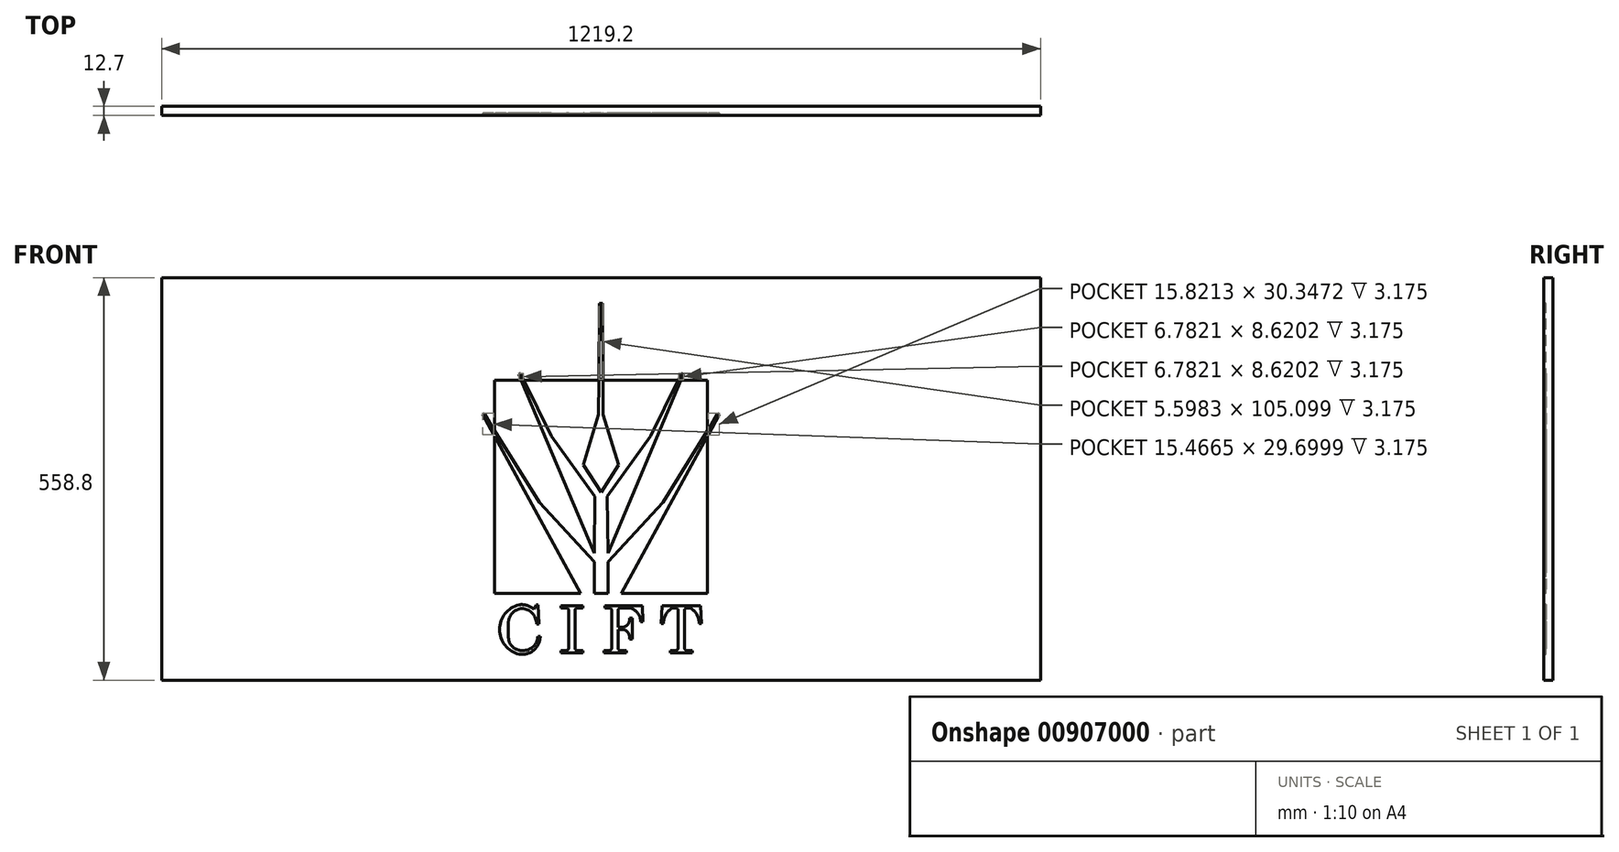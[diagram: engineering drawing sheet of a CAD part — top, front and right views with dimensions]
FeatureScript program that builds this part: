
annotation { "Feature Type Name" : "Feature", "Feature Type Description" : "" }
export const myFeature = defineFeature(function(context is Context, id is Id, definition is map)
    precondition{}
    {
        {
            var Q0;
            Q0=qCreatedBy(makeId("Front.planeOp"),FACE);
            var sketch = newSketch(context, id + "F0", { "sketchPlane" : qUnion([Q0])});
            skLineSegment(sketch, "E0.bottom", {"start": v(-609.6, 279.4) * mm, "end": v(609.6, 279.4) * mm});
            skLineSegment(sketch, "E0.top", {"start": v(-609.6, -279.4) * mm, "end": v(609.6, -279.4) * mm});
            skLineSegment(sketch, "E0.left", {"start": v(-609.6, 279.4) * mm, "end": v(-609.6, -279.4) * mm});
            skLineSegment(sketch, "E0.right", {"start": v(609.6, 279.4) * mm, "end": v(609.6, -279.4) * mm});
            skPoint(sketch, "E0.middle", {"position": v(0, 0) * mm});
            skSolve(sketch);
        }
        {
            var Q0;
            Q0=makeQuery(id+"F0.imprint","IMPRINT",FACE,{"disambiguationData":[TD([[makeQuery(id+"F0.imprint","IMPRINT",EDGE,{"derivedFrom":sQuery(id+"F0.wireOp",EDGE,"E0.bottom")}),-1.0]])]});
            extrude(context, id + "F1", {"entities" : qUnion([Q0]), "depth" : 12.7 * mm, "offsetDistance" : 25.4 * mm});
        }
        {
            var Q0;
            Q0=makeQuery(id+"F1.opExtrude","CAP_FACE",FACE,{"disambiguationData":[OSD([sQuery(id+"F0.wireOp",EDGE,"E0.bottom"),sQuery(id+"F0.wireOp",EDGE,"E0.top"),sQuery(id+"F0.wireOp",EDGE,"E0.left"),sQuery(id+"F0.wireOp",EDGE,"E0.right")])],"isStart":false});
            var sketch = newSketch(context, id + "F2", { "sketchPlane" : qUnion([Q0])});
            skLineSegment(sketch, "E1", {"start": v(-147.74, 136.91) * mm, "end": v(147.74, 136.91) * mm});
            skLineSegment(sketch, "E2", {"start": v(147.74, 136.91) * mm, "end": v(147.74, -158.78) * mm});
            skLineSegment(sketch, "E3", {"start": v(-148.88, 61.33) * mm, "end": v(-164.34, 89.54) * mm});
            skLineSegment(sketch, "E4", {"start": v(-161.78, 91.03) * mm, "end": v(-148.88, 68.77) * mm});
            skLineSegment(sketch, "E5", {"start": v(-85.66, -32.31) * mm, "end": v(-9.52, -115.33) * mm});
            skLineSegment(sketch, "E6", {"start": v(-9.52, -115.33) * mm, "end": v(-9.52, -158.78) * mm});
            skLineSegment(sketch, "E7", {"start": v(-164.34, 89.54) * mm, "end": v(-161.78, 91.03) * mm});
            skLineSegment(sketch, "E8", {"start": v(-114.28, 145.2) * mm, "end": v(-111.35, 146.3) * mm});
            skLineSegment(sketch, "E9", {"start": v(-111.35, 146.3) * mm, "end": v(-107.5, 137.68) * mm});
            skLineSegment(sketch, "E10", {"start": v(-68.91, 59.28) * mm, "end": v(-8.42, -24.15) * mm});
            skLineSegment(sketch, "E11", {"start": v(-8.42, -24.15) * mm, "end": v(-9.47, -102.91) * mm});
            skLineSegment(sketch, "E12", {"start": v(-111.1, 137.68) * mm, "end": v(-114.28, 145.2) * mm});
            skLineSegment(sketch, "E13", {"start": v(-0.06, -18.37) * mm, "end": v(-24.45, 19.7) * mm});
            skLineSegment(sketch, "E14", {"start": v(-24.45, 19.7) * mm, "end": v(-3.44, 89.6) * mm});
            skLineSegment(sketch, "E15", {"start": v(-3, 138.55) * mm, "end": v(-2.05, 243.65) * mm});
            skLineSegment(sketch, "E16", {"start": v(85.66, -32.31) * mm, "end": v(9.52, -115.33) * mm});
            skLineSegment(sketch, "E17", {"start": v(9.52, -115.33) * mm, "end": v(9.52, -158.78) * mm});
            skLineSegment(sketch, "E18", {"start": v(114.28, 145.2) * mm, "end": v(111.35, 146.3) * mm});
            skLineSegment(sketch, "E19", {"start": v(111.35, 146.3) * mm, "end": v(107.5, 137.68) * mm});
            skLineSegment(sketch, "E20", {"start": v(68.91, 59.28) * mm, "end": v(8.42, -24.15) * mm});
            skLineSegment(sketch, "E21", {"start": v(8.42, -24.15) * mm, "end": v(9.47, -102.91) * mm});
            skLineSegment(sketch, "E22", {"start": v(111.1, 137.68) * mm, "end": v(114.28, 145.2) * mm});
            skLineSegment(sketch, "E23", {"start": v(161.78, 91.03) * mm, "end": v(148.52, 68.16) * mm});
            skLineSegment(sketch, "E24", {"start": v(164.34, 89.54) * mm, "end": v(161.78, 91.03) * mm});
            skLineSegment(sketch, "E25", {"start": v(147.74, -158.78) * mm, "end": v(147.74, 136.91) * mm});
            skLineSegment(sketch, "E26", {"start": v(148.52, 60.68) * mm, "end": v(164.34, 89.54) * mm});
            skLineSegment(sketch, "E27", {"start": v(2.6, 138.55) * mm, "end": v(1.95, 243.65) * mm});
            skLineSegment(sketch, "E28", {"start": v(24.45, 19.7) * mm, "end": v(2.9, 89.6) * mm});
            skLineSegment(sketch, "E29", {"start": v(-147.74, -158.78) * mm, "end": v(-147.74, 136.91) * mm});
            skLineSegment(sketch, "E30", {"start": v(-0.06, -18.37) * mm, "end": v(24.45, 19.7) * mm});
            skLineSegment(sketch, "E31", {"start": v(-147.74, -158.78) * mm, "end": v(-28.22, -158.78) * mm});
            skLineSegment(sketch, "E32", {"start": v(28.22, -158.78) * mm, "end": v(147.74, -158.78) * mm});
            skLineSegment(sketch, "E33", {"start": v(-9.52, -158.78) * mm, "end": v(9.52, -158.78) * mm});
            skLineSegment(sketch, "E34", {"start": v(68.91, 59.28) * mm, "end": v(107.16, 136.91) * mm});
            skLineSegment(sketch, "E35", {"start": v(110.78, 136.91) * mm, "end": v(9.47, -102.91) * mm});
            skLineSegment(sketch, "E36", {"start": v(2.9, 89.6) * mm, "end": v(2.6, 136.91) * mm});
            skLineSegment(sketch, "E37", {"start": v(-3.01, 136.91) * mm, "end": v(-3.44, 89.6) * mm});
            skLineSegment(sketch, "E38", {"start": v(28.22, -158.78) * mm, "end": v(147.74, 59.25) * mm});
            skLineSegment(sketch, "E39", {"start": v(147.74, 66.8) * mm, "end": v(85.66, -32.31) * mm});
            skLineSegment(sketch, "E40", {"start": v(-68.91, 59.28) * mm, "end": v(-107.16, 136.91) * mm});
            skLineSegment(sketch, "E41", {"start": v(-110.78, 136.91) * mm, "end": v(-9.47, -102.91) * mm});
            skLineSegment(sketch, "E42", {"start": v(-85.66, -32.31) * mm, "end": v(-147.74, 66.8) * mm});
            skLineSegment(sketch, "E43", {"start": v(-147.74, 59.25) * mm, "end": v(-28.22, -158.78) * mm});
            skLineSegment(sketch, "E44", {"start": v(2.6, 136.91) * mm, "end": v(-3.01, 136.91) * mm});
            skLineSegment(sketch, "E45", {"start": v(110.78, 136.91) * mm, "end": v(107.16, 136.91) * mm});
            skLineSegment(sketch, "E46", {"start": v(147.74, 66.8) * mm, "end": v(147.74, 59.25) * mm});
            skLineSegment(sketch, "E47", {"start": v(-107.16, 136.91) * mm, "end": v(-110.78, 136.91) * mm});
            skLineSegment(sketch, "E48", {"start": v(-147.74, 59.25) * mm, "end": v(-147.74, 66.8) * mm});
            skArc(sketch, "E49", {"start": v(-89.4, -201.28) * mm, "mid": v(-95.36, -186.47) * mm, "end": v(-109.87, -179.83) * mm});
            skArc(sketch, "E50", {"start": v(-108.5, -238.28) * mm, "mid": v(-93.98, -232.57) * mm, "end": v(-87.6, -218.33) * mm});
            skLineSegment(sketch, "E51", {"start": v(-89.4, -201.28) * mm, "end": v(-86.08, -201.28) * mm});
            skLineSegment(sketch, "E52", {"start": v(-86.08, -201.28) * mm, "end": v(-87.23, -174.61) * mm});
            skLineSegment(sketch, "E53", {"start": v(-87.23, -174.61) * mm, "end": v(-90.18, -174.61) * mm});
            skLineSegment(sketch, "E54", {"start": v(-90.18, -174.61) * mm, "end": v(-93.08, -180.85) * mm});
            skLineSegment(sketch, "E55", {"start": v(-87.6, -218.33) * mm, "end": v(-84.44, -218.33) * mm});
            skArc(sketch, "E56", {"start": v(-128.45, -218.68) * mm, "mid": v(-122.82, -232.9) * mm, "end": v(-108.5, -238.28) * mm});
            skLineSegment(sketch, "E57", {"start": v(-55.67, -241.5) * mm, "end": v(-25.42, -241.5) * mm});
            skLineSegment(sketch, "E58", {"start": v(-55.67, -175.85) * mm, "end": v(-25.42, -175.85) * mm});
            skLineSegment(sketch, "E59", {"start": v(-55.67, -179.27) * mm, "end": v(-48.06, -179.27) * mm});
            skLineSegment(sketch, "E60", {"start": v(-55.67, -238.08) * mm, "end": v(-48.06, -238.08) * mm});
            skLineSegment(sketch, "E61", {"start": v(23.77, -205.82) * mm, "end": v(31.92, -205.82) * mm});
            skLineSegment(sketch, "E62", {"start": v(23.77, -209.24) * mm, "end": v(31.92, -209.24) * mm});
            skLineSegment(sketch, "E63", {"start": v(-45.08, -235.1) * mm, "end": v(-45.08, -182.24) * mm});
            skLineSegment(sketch, "E64", {"start": v(-35.9, -235.1) * mm, "end": v(-35.9, -182.24) * mm});
            skLineSegment(sketch, "E65", {"start": v(106.73, -235.1) * mm, "end": v(106.73, -182.24) * mm});
            skLineSegment(sketch, "E66", {"start": v(115.92, -235.1) * mm, "end": v(115.92, -182.24) * mm});
            skLineSegment(sketch, "E67", {"start": v(83.33, -200.72) * mm, "end": v(86.66, -200.72) * mm});
            skArc(sketch, "E68", {"start": v(98.5, -179.27) * mm, "mid": v(89.69, -188.4) * mm, "end": v(86.66, -200.72) * mm});
            skLineSegment(sketch, "E69", {"start": v(84.8, -175.85) * mm, "end": v(83.33, -200.72) * mm});
            skLineSegment(sketch, "E70", {"start": v(139.32, -200.72) * mm, "end": v(136, -200.72) * mm});
            skArc(sketch, "E71", {"start": v(136, -200.72) * mm, "mid": v(132.97, -188.4) * mm, "end": v(124.15, -179.27) * mm});
            skLineSegment(sketch, "E72", {"start": v(137.86, -175.85) * mm, "end": v(139.32, -200.72) * mm});
            skLineSegment(sketch, "E73", {"start": v(96.15, -241.5) * mm, "end": v(96.15, -238.08) * mm});
            skLineSegment(sketch, "E74", {"start": v(126.65, -241.5) * mm, "end": v(126.65, -238.08) * mm});
            skLineSegment(sketch, "E75", {"start": v(35.47, -241.5) * mm, "end": v(35.47, -238.08) * mm});
            skLineSegment(sketch, "E76", {"start": v(3.8, -241.5) * mm, "end": v(3.8, -238.08) * mm});
            skLineSegment(sketch, "E77", {"start": v(-25.42, -241.5) * mm, "end": v(-25.42, -238.08) * mm});
            skLineSegment(sketch, "E78", {"start": v(-55.67, -241.5) * mm, "end": v(-55.67, -238.08) * mm});
            skLineSegment(sketch, "E79", {"start": v(-55.67, -179.27) * mm, "end": v(-55.67, -175.85) * mm});
            skLineSegment(sketch, "E80", {"start": v(-25.42, -179.27) * mm, "end": v(-25.42, -175.85) * mm});
            skLineSegment(sketch, "E81", {"start": v(57.38, -175.85) * mm, "end": v(58.2, -198.56) * mm});
            skLineSegment(sketch, "E82", {"start": v(58.2, -198.56) * mm, "end": v(55, -198.56) * mm});
            skLineSegment(sketch, "E83", {"start": v(43.17, -222.7) * mm, "end": v(39.86, -222.7) * mm});
            skArc(sketch, "E84", {"start": v(39.86, -220.9) * mm, "mid": v(37.68, -213.85) * mm, "end": v(31.92, -209.24) * mm});
            skLineSegment(sketch, "E85", {"start": v(39.86, -222.7) * mm, "end": v(39.86, -220.9) * mm});
            skLineSegment(sketch, "E86", {"start": v(43.17, -222.7) * mm, "end": v(43.17, -193.2) * mm});
            skLineSegment(sketch, "E87", {"start": v(43.17, -193.2) * mm, "end": v(39.86, -193.2) * mm});
            skArc(sketch, "E88", {"start": v(-109.87, -179.83) * mm, "mid": v(-124.11, -187.5) * mm, "end": v(-128.45, -203.08) * mm});
            skArc(sketch, "E89", {"start": v(-113.64, -174.7) * mm, "mid": v(-140.74, -209.13) * mm, "end": v(-113.4, -243.36) * mm});
            skLineSegment(sketch, "E90", {"start": v(-128.45, -203.08) * mm, "end": v(-128.45, -218.68) * mm});
            skArc(sketch, "E91", {"start": v(-113.4, -243.36) * mm, "mid": v(-93.14, -237.53) * mm, "end": v(-84.44, -218.33) * mm});
            skArc(sketch, "E92", {"start": v(-93.08, -180.85) * mm, "mid": v(-102.7, -175.58) * mm, "end": v(-113.64, -174.7) * mm});
            skLineSegment(sketch, "E93", {"start": v(5.16, -175.83) * mm, "end": v(57.38, -175.85) * mm});
            skLineSegment(sketch, "E94", {"start": v(5.15, -179.25) * mm, "end": v(11.61, -179.25) * mm});
            skLineSegment(sketch, "E95", {"start": v(3.8, -238.08) * mm, "end": v(11.6, -238.08) * mm});
            skLineSegment(sketch, "E96", {"start": v(3.8, -241.5) * mm, "end": v(35.47, -241.5) * mm});
            skLineSegment(sketch, "E97", {"start": v(96.15, -238.08) * mm, "end": v(103.76, -238.08) * mm});
            skLineSegment(sketch, "E98", {"start": v(96.15, -241.5) * mm, "end": v(126.65, -241.5) * mm});
            skLineSegment(sketch, "E99", {"start": v(84.8, -175.85) * mm, "end": v(137.86, -175.85) * mm});
            skLineSegment(sketch, "E100", {"start": v(98.5, -179.27) * mm, "end": v(103.76, -179.27) * mm});
            skLineSegment(sketch, "E101", {"start": v(-32.92, -179.27) * mm, "end": v(-25.42, -179.27) * mm});
            skLineSegment(sketch, "E102", {"start": v(-32.92, -238.08) * mm, "end": v(-25.42, -238.08) * mm});
            skLineSegment(sketch, "E103", {"start": v(5.15, -179.25) * mm, "end": v(5.16, -175.83) * mm});
            skLineSegment(sketch, "E104", {"start": v(26.75, -179.26) * mm, "end": v(41.03, -179.26) * mm});
            skLineSegment(sketch, "E105", {"start": v(23.77, -235.1) * mm, "end": v(23.77, -209.24) * mm});
            skLineSegment(sketch, "E106", {"start": v(14.59, -235.1) * mm, "end": v(14.59, -182.23) * mm});
            skLineSegment(sketch, "E107", {"start": v(26.75, -238.08) * mm, "end": v(35.47, -238.08) * mm});
            skLineSegment(sketch, "E108", {"start": v(23.77, -205.82) * mm, "end": v(23.77, -182.23) * mm});
            skArc(sketch, "E109", {"start": v(31.92, -205.82) * mm, "mid": v(37.68, -201.2) * mm, "end": v(39.86, -194.15) * mm});
            skLineSegment(sketch, "E110", {"start": v(39.86, -194.15) * mm, "end": v(39.86, -193.2) * mm});
            skArc(sketch, "E111", {"start": v(55, -198.56) * mm, "mid": v(51.15, -186.64) * mm, "end": v(41.03, -179.26) * mm});
            skLineSegment(sketch, "E112", {"start": v(118.9, -179.27) * mm, "end": v(124.15, -179.27) * mm});
            skLineSegment(sketch, "E113", {"start": v(118.9, -238.08) * mm, "end": v(126.65, -238.08) * mm});
            skArc(sketch, "E114", {"start": v(-45.08, -182.24) * mm, "mid": v(-45.95, -180.14) * mm, "end": v(-48.06, -179.27) * mm});
            skArc(sketch, "E115", {"start": v(-32.92, -179.27) * mm, "mid": v(-35.02, -180.14) * mm, "end": v(-35.9, -182.24) * mm});
            skArc(sketch, "E116", {"start": v(-48.06, -238.08) * mm, "mid": v(-45.95, -237.2) * mm, "end": v(-45.08, -235.1) * mm});
            skArc(sketch, "E117", {"start": v(-35.9, -235.1) * mm, "mid": v(-35.02, -237.2) * mm, "end": v(-32.92, -238.08) * mm});
            skArc(sketch, "E118", {"start": v(23.77, -235.1) * mm, "mid": v(24.64, -237.2) * mm, "end": v(26.75, -238.08) * mm});
            skArc(sketch, "E119", {"start": v(11.6, -238.08) * mm, "mid": v(13.71, -237.2) * mm, "end": v(14.59, -235.1) * mm});
            skArc(sketch, "E120", {"start": v(26.75, -179.26) * mm, "mid": v(24.64, -180.13) * mm, "end": v(23.77, -182.23) * mm});
            skArc(sketch, "E121", {"start": v(14.59, -182.23) * mm, "mid": v(13.71, -180.12) * mm, "end": v(11.61, -179.25) * mm});
            skArc(sketch, "E122", {"start": v(118.9, -179.27) * mm, "mid": v(116.8, -180.14) * mm, "end": v(115.92, -182.24) * mm});
            skArc(sketch, "E123", {"start": v(106.73, -182.24) * mm, "mid": v(105.86, -180.14) * mm, "end": v(103.76, -179.27) * mm});
            skArc(sketch, "E124", {"start": v(115.92, -235.1) * mm, "mid": v(116.8, -237.2) * mm, "end": v(118.9, -238.08) * mm});
            skArc(sketch, "E125", {"start": v(103.76, -238.08) * mm, "mid": v(105.86, -237.2) * mm, "end": v(106.73, -235.1) * mm});
            skLineSegment(sketch, "E126", {"start": v(-2.05, 243.65) * mm, "end": v(1.95, 243.65) * mm});
            skLineSegment(sketch, "E127", {"start": v(-3, 138.55) * mm, "end": v(2.6, 138.55) * mm});
            skLineSegment(sketch, "E128.0", {"start": v(-111.1, 137.68) * mm, "end": v(-107.5, 137.68) * mm});
            skLineSegment(sketch, "E129.trimOffspring", {"start": v(107.5, 137.68) * mm, "end": v(111.1, 137.68) * mm});
            skLineSegment(sketch, "E130", {"start": v(-148.88, 68.77) * mm, "end": v(-148.88, 61.33) * mm});
            skLineSegment(sketch, "E131", {"start": v(148.52, 68.16) * mm, "end": v(148.52, 60.68) * mm});
            skSolve(sketch);
        }
        {
            var Q0;
            Q0=makeQuery(id+"F2.imprint","IMPRINT",FACE,{"disambiguationData":[TD([[makeQuery(id+"F2.imprint","IMPRINT",EDGE,{"derivedFrom":sQuery(id+"F2.wireOp",EDGE,"E5")}),1.0]])]});
            var Q1;
            {var subQ2=sQuery(id+"F2.wireOp",EDGE,"E31");Q1=makeQuery(id+"F2.imprint","IMPRINT",FACE,{"disambiguationData":[TD([[makeQuery(id+"F2.imprint","IMPRINT",EDGE,{"derivedFrom":subQ2}),1.0]])]});}
            var Q2;
            {var subQ0=sQuery(id+"F2.wireOp",EDGE,"E32");Q2=makeQuery(id+"F2.imprint","IMPRINT",FACE,{"disambiguationData":[TD([[makeQuery(id+"F2.imprint","IMPRINT",EDGE,{"derivedFrom":subQ0}),1.0]])]});}
            var Q3;
            Q3=makeQuery(id+"F2.imprint","IMPRINT",FACE,{"disambiguationData":[TD([[makeQuery(id+"F2.imprint","IMPRINT",EDGE,{"derivedFrom":sQuery(id+"F2.wireOp",EDGE,"E49")}),-1.0]])]});
            var Q4;
            Q4=makeQuery(id+"F2.imprint","IMPRINT",FACE,{"disambiguationData":[TD([[makeQuery(id+"F2.imprint","IMPRINT",EDGE,{"derivedFrom":sQuery(id+"F2.wireOp",EDGE,"E57")}),1.0]])]});
            var Q5;
            Q5=makeQuery(id+"F2.imprint","IMPRINT",FACE,{"disambiguationData":[TD([[makeQuery(id+"F2.imprint","IMPRINT",EDGE,{"derivedFrom":sQuery(id+"F2.wireOp",EDGE,"E61")}),-1.0]])]});
            var Q6;
            Q6=makeQuery(id+"F2.imprint","IMPRINT",FACE,{"disambiguationData":[TD([[makeQuery(id+"F2.imprint","IMPRINT",EDGE,{"derivedFrom":sQuery(id+"F2.wireOp",EDGE,"E65")}),-1.0]])]});
            var Q7;
            Q7=makeQuery(id+"F2.imprint","IMPRINT",FACE,{"disambiguationData":[TD([[makeQuery(id+"F2.imprint","IMPRINT",EDGE,{"derivedFrom":sQuery(id+"F2.wireOp",EDGE,"E15")}),-1.0]])]});
            var Q8;
            Q8=makeQuery(id+"F2.imprint","IMPRINT",FACE,{"disambiguationData":[TD([[makeQuery(id+"F2.imprint","IMPRINT",EDGE,{"derivedFrom":sQuery(id+"F2.wireOp",EDGE,"E3")}),-1.0]])]});
            var Q9;
            Q9=makeQuery(id+"F2.imprint","IMPRINT",FACE,{"disambiguationData":[TD([[makeQuery(id+"F2.imprint","IMPRINT",EDGE,{"derivedFrom":sQuery(id+"F2.wireOp",EDGE,"E8")}),-1.0]])]});
            var Q10;
            Q10=makeQuery(id+"F2.imprint","IMPRINT",FACE,{"disambiguationData":[TD([[makeQuery(id+"F2.imprint","IMPRINT",EDGE,{"derivedFrom":sQuery(id+"F2.wireOp",EDGE,"E18")}),1.0]])]});
            var Q11;
            Q11=makeQuery(id+"F2.imprint","IMPRINT",FACE,{"disambiguationData":[TD([[makeQuery(id+"F2.imprint","IMPRINT",EDGE,{"derivedFrom":sQuery(id+"F2.wireOp",EDGE,"E23")}),1.0]])]});
            extrude(context, id + "F3", {"entities" : qUnion([Q0, Q1, Q2, Q3, Q4, Q5, Q6, Q7, Q8, Q9, Q10, Q11]), "operationType" : NewBodyOperationType.REMOVE, "oppositeDirection" : true, "depth" : 3.17 * mm, "offsetDistance" : 25.4 * mm});
        }
    });
